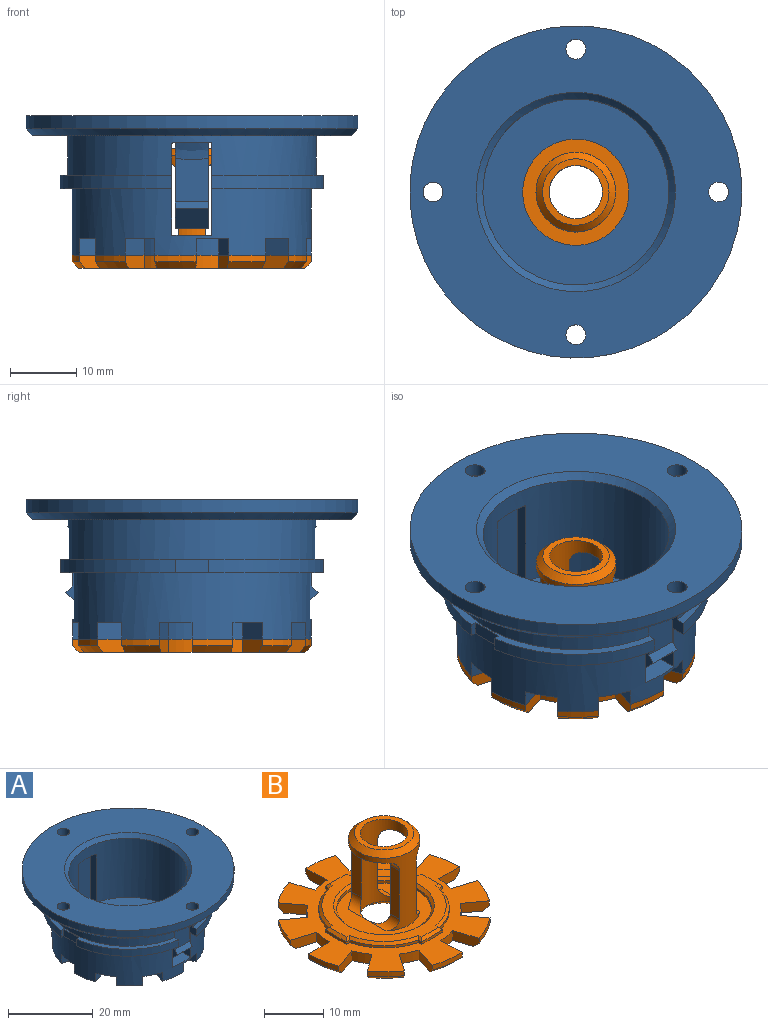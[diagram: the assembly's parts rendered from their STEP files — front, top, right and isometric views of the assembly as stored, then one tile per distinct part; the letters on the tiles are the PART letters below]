
ASSEMBLY  parts=2 mates=1
PART A: 120 faces, bbox 50.1x50.1x21.1 mm
  f0: cylinder r=20mm len=17.27mm, axis (0,0,-1), area 51.8mm2, adj f1,f6,f81,f117
  f1: plane 39.55x16.84mm, normal (0,0,-1), area 102.6mm2, adj f0,f7,f8,f77,f81,f117,f118,f119
  f2: plane 39.55x16.84mm, normal (0,0,1), area 63.8mm2, adj f3,f56,f74,f78,f80,f114,f115,f116
  f3: cylinder r=20mm len=17.27mm, axis (0,0,-1), area 51.8mm2, adj f2,f4,f78,f115
  f4: plane 39.55x16.84mm, normal (0,0,-1), area 102.6mm2, adj f3,f8,f74,f78,f80,f114,f115,f116
  f5: plane 5.54x4.83mm, normal (0,0,-1), area 6.3mm2, adj f51,f56,f91,f98,f99,f104,f105
  f6: plane 39.55x16.84mm, normal (0,0,1), area 63.8mm2, adj f0,f7,f56,f77,f81,f117,f118,f119
  f7: cylinder r=20mm len=17.27mm, axis (0,0,-1), area 51.8mm2, adj f1,f6,f77,f118
  f8: cylinder r=18mm len=36mm, axis (0,0,-1), area 921.2mm2, adj f1,f4,f10,f11,f13,f14,f15,f17
  f9: cylinder r=8mm len=16mm, axis (0,0,-1), area 50.3mm2, adj f52,f73
  f10: plane 36x36mm, normal (0,0,-1), area 411.8mm2, adj f8,f11,f12,f13,f15,f16,f17,f19
  f11: plane 5x2.5mm, normal (0,-1,0), area 12.5mm2, adj f8,f10,f12,f14
  f12: cylinder r=13mm len=3.5mm, axis (0,0,-1), area 8.9mm2, adj f10,f11,f13,f14
  f13: plane 4.79x2.5mm, normal (0.29,0.96,0), area 12.5mm2, adj f8,f10,f12,f14
  f14: plane 5.48x4.95mm, normal (0,0,-1), area 21.4mm2, adj f8,f11,f12,f13
  f15: plane 4.05x2.94mm, normal (0.59,-0.81,0), area 12.5mm2, adj f8,f10,f16,f18
  f16: cylinder r=13mm len=3.11mm, axis (0,0,-1), area 8.9mm2, adj f10,f15,f17,f18
  f17: plane 4.73x2.5mm, normal (-0.33,0.94,0), area 12.5mm2, adj f8,f10,f16,f18
  f18: plane 6.39x6.05mm, normal (0,0,-1), area 21.4mm2, adj f8,f15,f16,f17
  f19: plane 4.76x2.5mm, normal (0.95,-0.31,0), area 12.5mm2, adj f8,f10,f20,f22
  f20: cylinder r=13mm len=3.18mm, axis (0,0,-1), area 8.9mm2, adj f10,f19,f21,f22
  f21: plane 4.1x2.86mm, normal (-0.82,0.57,0), area 12.5mm2, adj f8,f10,f20,f22
  f22: plane 6.29x6.04mm, normal (0,0,-1), area 21.4mm2, adj f8,f19,f20,f21
  f23: plane 4.76x2.5mm, normal (0.95,0.31,0), area 12.5mm2, adj f8,f10,f24,f26
  f24: cylinder r=13mm len=3.48mm, axis (0,0,-1), area 8.9mm2, adj f10,f23,f25,f26
  f25: plane 5x2.5mm, normal (-1,-0.02,0), area 12.5mm2, adj f8,f10,f24,f26
  f26: plane 5.63x5.02mm, normal (0,0,-1), area 21.4mm2, adj f8,f23,f24,f25
  f27: plane 4.05x2.94mm, normal (0.59,0.81,0), area 12.5mm2, adj f8,f10,f28,f30
  f28: cylinder r=13mm len=2.55mm, axis (0,0,-1), area 8.9mm2, adj f10,f27,f29,f30
  f29: plane 3.99x3.02mm, normal (-0.8,-0.6,0), area 12.5mm2, adj f8,f10,f28,f30
  f30: plane 6.54x6.49mm, normal (0,0,-1), area 21.4mm2, adj f8,f27,f28,f29
  f31: plane 5x2.5mm, normal (0,1,0), area 12.5mm2, adj f8,f10,f32,f34
  f32: cylinder r=13mm len=3.5mm, axis (0,0,-1), area 8.9mm2, adj f10,f31,f33,f34
  f33: plane 4.79x2.5mm, normal (-0.29,-0.96,0), area 12.5mm2, adj f8,f10,f32,f34
  f34: plane 5.48x4.95mm, normal (0,0,-1), area 21.4mm2, adj f8,f31,f32,f33
  f35: plane 4.05x2.94mm, normal (-0.59,0.81,0), area 12.5mm2, adj f8,f10,f36,f38
  f36: cylinder r=13mm len=3.11mm, axis (0,0,-1), area 8.9mm2, adj f10,f35,f37,f38
  f37: plane 4.73x2.5mm, normal (0.33,-0.94,0), area 12.5mm2, adj f8,f10,f36,f38
  f38: plane 6.39x6.05mm, normal (0,0,-1), area 21.4mm2, adj f8,f35,f36,f37
  f39: plane 4.76x2.5mm, normal (-0.95,0.31,0), area 12.5mm2, adj f8,f10,f40,f42
  f40: cylinder r=13mm len=3.18mm, axis (0,0,-1), area 8.9mm2, adj f10,f39,f41,f42
  f41: plane 4.1x2.86mm, normal (0.82,-0.57,0), area 12.5mm2, adj f8,f10,f40,f42
  f42: plane 6.29x6.04mm, normal (0,0,-1), area 21.4mm2, adj f8,f39,f40,f41
  f43: plane 4.76x2.5mm, normal (-0.95,-0.31,0), area 12.5mm2, adj f8,f10,f44,f46
  f44: cylinder r=13mm len=3.48mm, axis (0,0,-1), area 8.9mm2, adj f10,f43,f45,f46
  f45: plane 5x2.5mm, normal (1,0.02,0), area 12.5mm2, adj f8,f10,f44,f46
  f46: plane 5.63x5.02mm, normal (0,0,-1), area 21.4mm2, adj f8,f43,f44,f45
  f47: plane 4.05x2.94mm, normal (-0.59,-0.81,0), area 12.5mm2, adj f8,f10,f48,f50
  f48: cylinder r=13mm len=2.55mm, axis (0,0,-1), area 8.9mm2, adj f10,f47,f49,f50
  f49: plane 3.99x3.02mm, normal (0.8,0.6,0), area 12.5mm2, adj f8,f10,f48,f50
  f50: plane 6.54x6.49mm, normal (0,0,-1), area 21.4mm2, adj f8,f47,f48,f49
  f51: cylinder r=14mm len=28mm, axis (0,0,-1), area 1326.2mm2, adj f5,f52,f76,f77,f78,f79,f80,f81
  f52: plane 36x28mm, normal (0,0,1), area 463mm2, adj f8,f9,f51,f77,f78,f80,f81
  f53: cylinder r=25mm len=50mm, axis (0,0,-1), area 314.2mm2, adj f54,f75
  f54: plane 50x50mm, normal (0,0,1), area 1228.4mm2, adj f53,f76,f106,f107,f108,f109
  f55: plane 48x48mm, normal (0,0,-1), area 626.6mm2, adj f56,f75,f110,f111,f112,f113
  f56: cylinder r=18.75mm len=37.5mm, axis (0,0,-1), area 646.6mm2, adj f2,f5,f6,f55,f77,f78,f79,f80
  f57: plane 2x0.79mm, normal (1,0,0), area 1.6mm2, adj f10,f58,f72,f73
  f58: cylinder r=11mm len=8.21mm, axis (0,0,-1), area 24.5mm2, adj f10,f57,f59,f73
  f59: plane 2x0.79mm, normal (0,-1,0), area 1.6mm2, adj f10,f58,f60,f73
  f60: plane 5x2mm, normal (1,0,0), area 10mm2, adj f10,f59,f61,f73
  f61: plane 2x0.79mm, normal (0,1,0), area 1.6mm2, adj f10,f60,f62,f73
  f62: cylinder r=11mm len=8.21mm, axis (0,0,-1), area 24.5mm2, adj f10,f61,f63,f73
  f63: plane 2x0.79mm, normal (1,0,0), area 1.6mm2, adj f10,f62,f64,f73
  f64: plane 5x2mm, normal (0,1,0), area 10mm2, adj f10,f63,f65,f73
  f65: plane 2x0.79mm, normal (-1,0,0), area 1.6mm2, adj f10,f64,f66,f73
  f66: cylinder r=11mm len=8.21mm, axis (0,0,-1), area 24.5mm2, adj f10,f65,f67,f73
  f67: plane 2x0.79mm, normal (0,1,0), area 1.6mm2, adj f10,f66,f68,f73
  f68: plane 5x2mm, normal (-1,0,0), area 10mm2, adj f10,f67,f69,f73
  f69: plane 2x0.79mm, normal (0,-1,0), area 1.6mm2, adj f10,f68,f70,f73
  f70: cylinder r=11mm len=8.21mm, axis (0,0,-1), area 24.5mm2, adj f10,f69,f71,f73
  f71: plane 2x0.79mm, normal (-1,0,0), area 1.6mm2, adj f10,f70,f72,f73
  f72: plane 5x2mm, normal (0,-1,0), area 10mm2, adj f10,f57,f71,f73
  f73: plane 23x23mm, normal (0,0,-1), area 191mm2, adj f9,f57,f58,f59,f60,f61,f62,f63
  f74: cylinder r=20mm len=17.27mm, axis (0,0,-1), area 51.8mm2, adj f2,f4,f80,f114
  f75: cone r=25mm half-angle=45deg, axis (0,0,1), area 217.7mm2, adj f53,f55
  f76: cone r=14mm half-angle=45deg, axis (0,0,1), area 128.8mm2, adj f51,f54
  f77: plane 13.77x6.1mm, normal (1,0,0), area 63.8mm2, adj f1,f6,f7,f8,f51,f52,f56,f105
  f78: plane 13.77x6.1mm, normal (-1,0,0), area 63.8mm2, adj f2,f3,f4,f8,f51,f52,f56,f104
  f79: plane 5.54x4.83mm, normal (0,0,-1), area 6.3mm2, adj f51,f56,f86,f100,f101,f102,f103
  f80: plane 13.77x6.1mm, normal (-1,0,0), area 63.8mm2, adj f2,f4,f8,f51,f52,f56,f74,f102
  f81: plane 13.77x6.1mm, normal (1,0,0), area 63.8mm2, adj f0,f1,f6,f8,f51,f52,f56,f103
  f82: plane 12.84x4.07mm, normal (-1,0,0), area 37.6mm2, adj f83,f85,f86,f92,f96,f97,f100
  f83: plane 5x1mm, normal (0,0,-1), area 5mm2, adj f82,f84,f86,f97
  f84: plane 12.83x4.06mm, normal (1,0,0), area 37.6mm2, adj f83,f85,f86,f92,f96,f97,f101
  f85: plane 6.6x5mm, normal (0,-1,0), area 32.2mm2, adj f82,f84,f92,f96
  f86: plane 13x5.46mm, normal (0,1,0), area 65mm2, adj f79,f82,f83,f84,f100,f101
  f87: plane 12.83x4.06mm, normal (-1,0,0), area 37.6mm2, adj f88,f90,f91,f93,f94,f95,f98
  f88: plane 5x1mm, normal (0,0,-1), area 5mm2, adj f87,f89,f91,f94
  f89: plane 12.84x4.07mm, normal (1,0,0), area 37.6mm2, adj f88,f90,f91,f93,f94,f95,f99
  f90: plane 6.6x5mm, normal (0,1,0), area 32.2mm2, adj f87,f89,f93,f95
  f91: plane 13x5.46mm, normal (0,-1,0), area 65mm2, adj f5,f87,f88,f89,f98,f99
  f92: bspline ~6.77x2.63mm, area 13.5mm2, adj f56,f82,f84,f85,f100,f101
  f93: bspline ~6.77x2.63mm, area 13.5mm2, adj f56,f87,f89,f90,f98,f99
  f94: plane 5x3mm, normal (0,0.71,-0.71), area 21.2mm2, adj f87,f88,f89,f95
  f95: plane 5x1mm, normal (0,0.71,0.71), area 7.1mm2, adj f87,f89,f90,f94
  f96: plane 5x1mm, normal (0,-0.71,0.71), area 7.1mm2, adj f82,f84,f85,f97
  f97: plane 5x3mm, normal (0,-0.71,-0.71), area 21.2mm2, adj f82,f83,f84,f96
  f98: cylinder r=0.23mm len=3.55mm, axis (0,-1,0), area 1.3mm2, adj f5,f87,f91,f93
  f99: cylinder r=0.23mm len=3.55mm, axis (0,1,0), area 1.3mm2, adj f5,f89,f91,f93
  f100: cylinder r=0.23mm len=3.55mm, axis (0,-1,0), area 1.3mm2, adj f79,f82,f86,f92
  f101: cylinder r=0.23mm len=3.55mm, axis (0,1,0), area 1.3mm2, adj f79,f84,f86,f92
  f102: cylinder r=0.23mm len=4.87mm, axis (0,1,0), area 1.7mm2, adj f51,f56,f79,f80
  f103: cylinder r=0.23mm len=4.87mm, axis (0,-1,0), area 1.7mm2, adj f51,f56,f79,f81
  f104: cylinder r=0.23mm len=4.87mm, axis (0,1,0), area 1.7mm2, adj f5,f51,f56,f78
  f105: cylinder r=0.23mm len=4.87mm, axis (0,-1,0), area 1.7mm2, adj f5,f51,f56,f77
  f106: cylinder r=1.5mm len=3mm, axis (0,0,-1), area 18.8mm2, adj f54,f111
  f107: cylinder r=1.5mm len=3mm, axis (0,0,-1), area 18.8mm2, adj f54,f110
  f108: cylinder r=1.5mm len=3mm, axis (0,0,-1), area 18.8mm2, adj f54,f113
  f109: cylinder r=1.5mm len=3mm, axis (0,0,-1), area 18.8mm2, adj f54,f112
  f110: cone r=1.5mm half-angle=45deg, axis (0,0,-1), area 17.8mm2, adj f55,f107
  f111: cone r=1.5mm half-angle=45deg, axis (0,0,-1), area 17.8mm2, adj f55,f106
  f112: cone r=1.5mm half-angle=45deg, axis (0,0,-1), area 17.8mm2, adj f55,f109
  f113: cone r=1.5mm half-angle=45deg, axis (0,0,-1), area 17.8mm2, adj f55,f108
  f114: plane 2x0.84mm, normal (0,1,0), area 1.7mm2, adj f2,f4,f74,f116
  f115: plane 2x0.84mm, normal (0,-1,0), area 1.7mm2, adj f2,f3,f4,f116
  f116: plane 5x2mm, normal (1,0,0), area 10mm2, adj f2,f4,f114,f115
  f117: plane 2x0.84mm, normal (0,1,0), area 1.7mm2, adj f0,f1,f6,f119
  f118: plane 2x0.84mm, normal (0,-1,0), area 1.7mm2, adj f1,f6,f7,f119
  f119: plane 5x2mm, normal (-1,0,0), area 10mm2, adj f1,f6,f117,f118
PART B: 107 faces, bbox 36x36x18 mm
  f0: plane 16x16mm, normal (0,0,1), area 112.7mm2, adj f1,f63,f64,f65,f66,f88
  f1: cylinder r=6mm len=15mm, axis (0,0,-1), area 159.4mm2, adj f0,f57,f58,f59,f60,f61,f62,f63
  f2: cylinder r=18mm len=5.53mm, axis (0,0,1), area 6.3mm2, adj f14,f23,f48,f53
  f3: cylinder r=18mm len=6.2mm, axis (0,0,1), area 6.3mm2, adj f15,f23,f45,f50
  f4: cylinder r=18mm len=4.51mm, axis (0,0,1), area 6.3mm2, adj f16,f23,f42,f47
  f5: cylinder r=18mm len=6.17mm, axis (0,0,1), area 6.3mm2, adj f17,f23,f39,f44
  f6: cylinder r=18mm len=5.63mm, axis (0,0,1), area 6.3mm2, adj f18,f23,f36,f41
  f7: cylinder r=18mm len=5.53mm, axis (0,0,1), area 6.3mm2, adj f19,f23,f33,f38
  f8: cylinder r=18mm len=6.2mm, axis (0,0,1), area 6.3mm2, adj f20,f23,f30,f35
  f9: cylinder r=18mm len=4.51mm, axis (0,0,1), area 6.3mm2, adj f21,f23,f27,f32
  f10: cylinder r=18mm len=6.17mm, axis (0,0,1), area 6.3mm2, adj f22,f23,f24,f29
  f11: cylinder r=18mm len=5.63mm, axis (0,0,1), area 6.3mm2, adj f13,f23,f26,f51
  f12: plane 34x34mm, normal (0,0,-1), area 664.1mm2, adj f13,f14,f15,f16,f17,f18,f19,f20
  f13: cone r=18mm half-angle=45deg, axis (0,0,1), area 8.7mm2, adj f11,f12,f26,f51
  f14: cone r=18mm half-angle=45deg, axis (0,0,1), area 8.7mm2, adj f2,f12,f48,f53
  f15: cone r=18mm half-angle=45deg, axis (0,0,1), area 8.7mm2, adj f3,f12,f45,f50
  f16: cone r=18mm half-angle=45deg, axis (0,0,1), area 8.7mm2, adj f4,f12,f42,f47
  f17: cone r=18mm half-angle=45deg, axis (0,0,1), area 8.7mm2, adj f5,f12,f39,f44
  f18: cone r=18mm half-angle=45deg, axis (0,0,1), area 8.7mm2, adj f6,f12,f36,f41
  f19: cone r=18mm half-angle=45deg, axis (0,0,1), area 8.7mm2, adj f7,f12,f33,f38
  f20: cone r=18mm half-angle=45deg, axis (0,0,1), area 8.7mm2, adj f8,f12,f30,f35
  f21: cone r=18mm half-angle=45deg, axis (0,0,1), area 8.7mm2, adj f9,f12,f27,f32
  f22: cone r=18mm half-angle=45deg, axis (0,0,1), area 8.7mm2, adj f10,f12,f24,f29
  f23: plane 36x36mm, normal (0,0,1), area 411.8mm2, adj f2,f3,f4,f5,f6,f7,f8,f9
  f24: plane 5x2mm, normal (0,-1,0), area 9.5mm2, adj f10,f12,f22,f23,f25
  f25: cylinder r=13mm len=3.5mm, axis (0,0,1), area 7.1mm2, adj f12,f23,f24,f26
  f26: plane 4.79x2mm, normal (0.29,0.96,0), area 9.5mm2, adj f11,f12,f13,f23,f25
  f27: plane 4.05x2.94mm, normal (0.59,-0.81,0), area 9.5mm2, adj f9,f12,f21,f23,f28
  f28: cylinder r=13mm len=3.11mm, axis (0,0,1), area 7.1mm2, adj f12,f23,f27,f29
  f29: plane 4.73x2mm, normal (-0.33,0.94,0), area 9.5mm2, adj f10,f12,f22,f23,f28
  f30: plane 4.76x2mm, normal (0.95,-0.31,0), area 9.5mm2, adj f8,f12,f20,f23,f31
  f31: cylinder r=13mm len=3.18mm, axis (0,0,1), area 7.1mm2, adj f12,f23,f30,f32
  f32: plane 4.1x2.86mm, normal (-0.82,0.57,0), area 9.5mm2, adj f9,f12,f21,f23,f31
  f33: plane 4.76x2mm, normal (0.95,0.31,0), area 9.5mm2, adj f7,f12,f19,f23,f34
  f34: cylinder r=13mm len=3.48mm, axis (0,0,1), area 7.1mm2, adj f12,f23,f33,f35
  f35: plane 5x2mm, normal (-1,-0.02,0), area 9.5mm2, adj f8,f12,f20,f23,f34
  f36: plane 4.05x2.94mm, normal (0.59,0.81,0), area 9.5mm2, adj f6,f12,f18,f23,f37
  f37: cylinder r=13mm len=2.55mm, axis (0,0,1), area 7.1mm2, adj f12,f23,f36,f38
  f38: plane 3.99x3.02mm, normal (-0.8,-0.6,0), area 9.5mm2, adj f7,f12,f19,f23,f37
  f39: plane 5x2mm, normal (0,1,0), area 9.5mm2, adj f5,f12,f17,f23,f40
  f40: cylinder r=13mm len=3.5mm, axis (0,0,1), area 7.1mm2, adj f12,f23,f39,f41
  f41: plane 4.79x2mm, normal (-0.29,-0.96,0), area 9.5mm2, adj f6,f12,f18,f23,f40
  f42: plane 4.05x2.94mm, normal (-0.59,0.81,0), area 9.5mm2, adj f4,f12,f16,f23,f43
  f43: cylinder r=13mm len=3.11mm, axis (0,0,1), area 7.1mm2, adj f12,f23,f42,f44
  f44: plane 4.73x2mm, normal (0.33,-0.94,0), area 9.5mm2, adj f5,f12,f17,f23,f43
  f45: plane 4.76x2mm, normal (-0.95,0.31,0), area 9.5mm2, adj f3,f12,f15,f23,f46
  f46: cylinder r=13mm len=3.18mm, axis (0,0,1), area 7.1mm2, adj f12,f23,f45,f47
  f47: plane 4.1x2.86mm, normal (0.82,-0.57,0), area 9.5mm2, adj f4,f12,f16,f23,f46
  f48: plane 4.76x2mm, normal (-0.95,-0.31,0), area 9.5mm2, adj f2,f12,f14,f23,f49
  f49: cylinder r=13mm len=3.48mm, axis (0,0,1), area 7.1mm2, adj f12,f23,f48,f50
  f50: plane 5x2mm, normal (1,0.02,0), area 9.5mm2, adj f3,f12,f15,f23,f49
  f51: plane 4.05x2.94mm, normal (-0.59,-0.81,0), area 9.5mm2, adj f11,f12,f13,f23,f52
  f52: cylinder r=13mm len=2.55mm, axis (0,0,1), area 7.1mm2, adj f12,f23,f51,f53
  f53: plane 3.99x3.02mm, normal (0.8,0.6,0), area 9.5mm2, adj f2,f12,f14,f23,f52
  f54: cylinder r=4mm len=17mm, axis (0,0,1), area 201.6mm2, adj f55,f56,f57,f58,f60,f61,f63,f64
  f55: plane 10x10mm, normal (0,0,1), area 28.3mm2, adj f54,f67
  f56: cone r=5mm half-angle=45deg, axis (0,0,-1), area 40mm2, adj f12,f54
  f57: plane 10x2.19mm, normal (-1,0,0), area 21.9mm2, adj f1,f54,f65,f70
  f58: plane 10x2.19mm, normal (-1,0,0), area 21.9mm2, adj f1,f54,f64,f69
  f59: plane 8.94x2mm, normal (0,0,-1), area 12.4mm2, adj f1,f69,f70
  f60: plane 10x2.19mm, normal (1,0,0), area 21.9mm2, adj f1,f54,f66,f71
  f61: plane 10x2.19mm, normal (1,0,0), area 21.9mm2, adj f1,f54,f63,f68
  f62: plane 8.94x2mm, normal (0,0,-1), area 12.4mm2, adj f1,f68,f71
  f63: cylinder r=2mm len=5.66mm, axis (0,1,0), area 8mm2, adj f0,f1,f54,f61
  f64: cylinder r=2mm len=5.66mm, axis (0,-1,0), area 8mm2, adj f0,f1,f54,f58
  f65: cylinder r=2mm len=5.66mm, axis (0,-1,0), area 8mm2, adj f0,f1,f54,f57
  f66: cylinder r=2mm len=5.66mm, axis (0,1,0), area 8mm2, adj f0,f1,f54,f60
  f67: cone r=5mm half-angle=45deg, axis (0,0,-1), area 48.9mm2, adj f1,f55
  f68: cylinder r=2mm len=5.66mm, axis (0,-1,0), area 8mm2, adj f1,f54,f61,f62
  f69: cylinder r=2mm len=5.66mm, axis (0,1,0), area 8mm2, adj f1,f54,f58,f59
  f70: cylinder r=2mm len=5.66mm, axis (0,1,0), area 8mm2, adj f1,f54,f57,f59
  f71: cylinder r=2mm len=5.66mm, axis (0,-1,0), area 8mm2, adj f1,f54,f60,f62
  f72: plane 0.79x0.5mm, normal (-1,0,0), area 0.4mm2, adj f23,f73,f87,f94
  f73: cylinder r=11mm len=8.21mm, axis (0,0,-1), area 6.1mm2, adj f23,f72,f74,f92
  f74: plane 0.79x0.5mm, normal (0,1,0), area 0.4mm2, adj f23,f73,f75,f90
  f75: plane 5x0.5mm, normal (-1,0,0), area 2.5mm2, adj f23,f74,f76,f91
  f76: plane 0.79x0.5mm, normal (0,-1,0), area 0.4mm2, adj f23,f75,f77,f93
  f77: cylinder r=11mm len=8.21mm, axis (0,0,-1), area 6.1mm2, adj f23,f76,f78,f95
  f78: plane 0.79x0.5mm, normal (-1,0,0), area 0.4mm2, adj f23,f77,f79,f97
  f79: plane 5x0.5mm, normal (0,-1,0), area 2.5mm2, adj f23,f78,f80,f99
  f80: plane 0.79x0.5mm, normal (1,0,0), area 0.4mm2, adj f23,f79,f81,f101
  f81: cylinder r=11mm len=8.21mm, axis (0,0,-1), area 6.1mm2, adj f23,f80,f82,f103
  f82: plane 0.79x0.5mm, normal (0,-1,0), area 0.4mm2, adj f23,f81,f83,f105
  f83: plane 5x0.5mm, normal (1,0,0), area 2.5mm2, adj f23,f82,f84,f104
  f84: plane 0.79x0.5mm, normal (0,1,0), area 0.4mm2, adj f23,f83,f85,f102
  f85: cylinder r=11mm len=8.21mm, axis (0,0,-1), area 6.1mm2, adj f23,f84,f86,f100
  f86: plane 0.79x0.5mm, normal (1,0,0), area 0.4mm2, adj f23,f85,f87,f98
  f87: plane 5x0.5mm, normal (0,1,0), area 2.5mm2, adj f23,f72,f86,f96
  f88: cylinder r=8mm len=16mm, axis (0,0,-1), area 25.1mm2, adj f0,f106
  f89: plane 22x22mm, normal (0,0,1), area 128.4mm2, adj f90,f91,f92,f93,f94,f95,f96,f97
  f90: plane 1.2x0.51mm, normal (0,0.71,0.71), area 0.5mm2, adj f74,f89,f91,f92
  f91: plane 5x0.5mm, normal (-0.71,0,0.71), area 3.2mm2, adj f75,f89,f90,f93
  f92: cone r=10.5mm half-angle=45deg, axis (0,0,-1), area 8.7mm2, adj f73,f89,f90,f94
  f93: plane 1.2x0.51mm, normal (0,-0.71,0.71), area 0.5mm2, adj f76,f89,f91,f95
  f94: plane 1.2x0.51mm, normal (-0.71,0,0.71), area 0.5mm2, adj f72,f89,f92,f96
  f95: cone r=10.5mm half-angle=45deg, axis (0,0,-1), area 8.7mm2, adj f77,f89,f93,f97
  f96: plane 5x0.5mm, normal (0,0.71,0.71), area 3.2mm2, adj f87,f89,f94,f98
  f97: plane 1.2x0.51mm, normal (-0.71,0,0.71), area 0.5mm2, adj f78,f89,f95,f99
  f98: plane 1.2x0.51mm, normal (0.71,0,0.71), area 0.5mm2, adj f86,f89,f96,f100
  f99: plane 5x0.5mm, normal (0,-0.71,0.71), area 3.2mm2, adj f79,f89,f97,f101
  f100: cone r=10.5mm half-angle=45deg, axis (0,0,-1), area 8.7mm2, adj f85,f89,f98,f102
  f101: plane 1.2x0.51mm, normal (0.71,0,0.71), area 0.5mm2, adj f80,f89,f99,f103
  f102: plane 1.2x0.51mm, normal (0,0.71,0.71), area 0.5mm2, adj f84,f89,f100,f104
  f103: cone r=10.5mm half-angle=45deg, axis (0,0,-1), area 8.7mm2, adj f81,f89,f101,f105
  f104: plane 5x0.5mm, normal (0.71,0,0.71), area 3.2mm2, adj f83,f89,f102,f105
  f105: plane 1.2x0.51mm, normal (0,-0.71,0.71), area 0.5mm2, adj f82,f89,f103,f104
  f106: cone r=8mm half-angle=45deg, axis (0,0,1), area 36.7mm2, adj f88,f89
PLACE A t=(0.06,0,-12.23)mm
PLACE B t=(0.06,0,-12.23)mm
MATE fastened A.f10 <-> B.f23  axis (0,0,-1) through (-17.94,0,-12.23)mm
